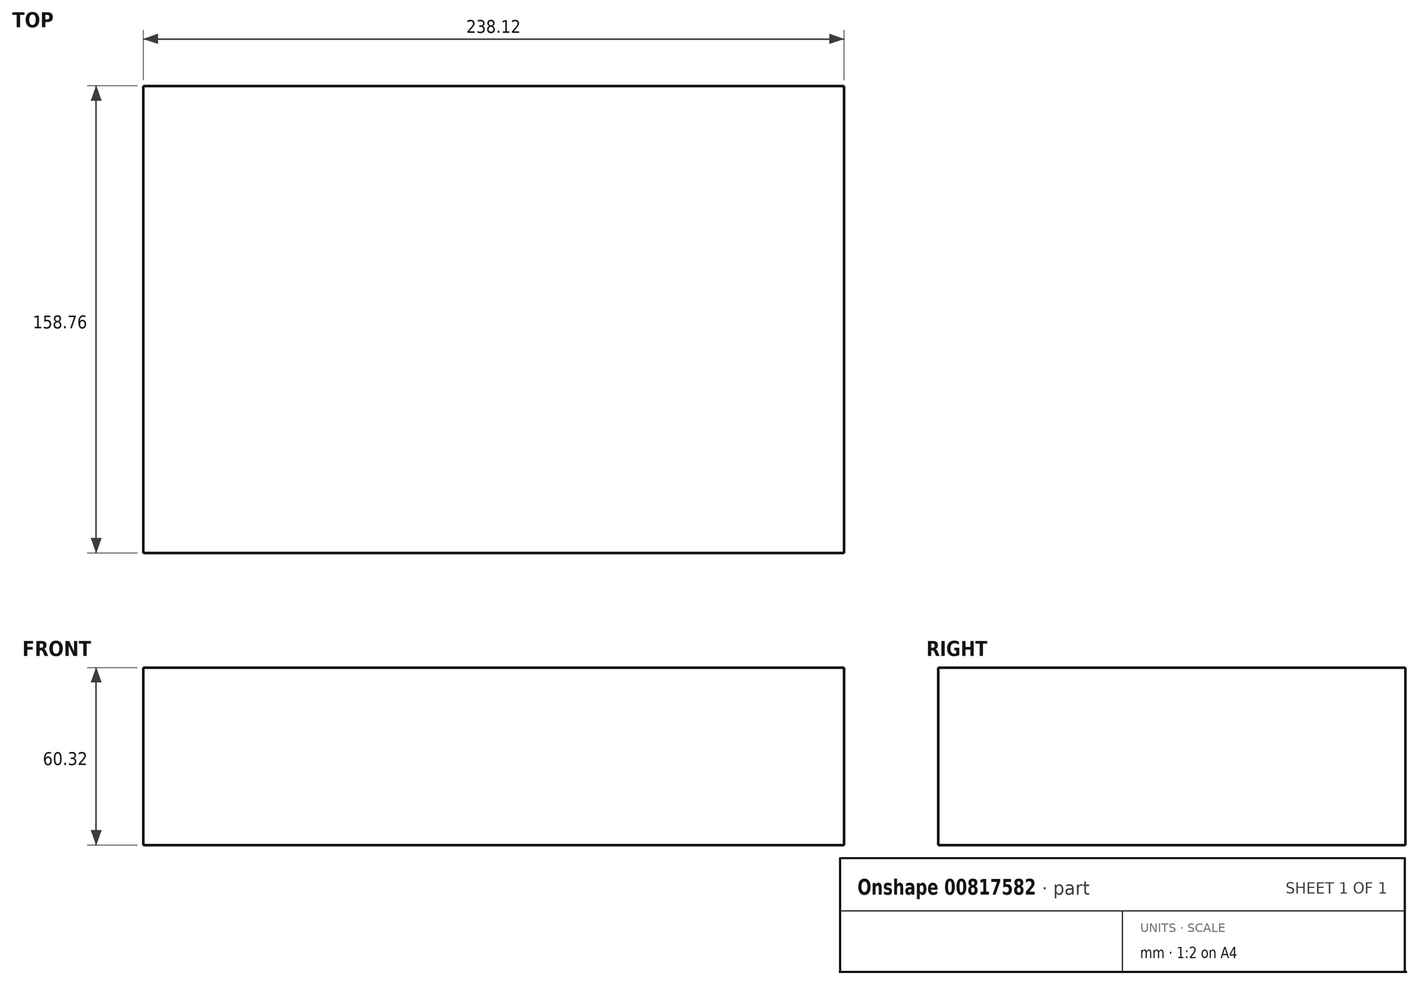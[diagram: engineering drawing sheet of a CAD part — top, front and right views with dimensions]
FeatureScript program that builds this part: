
annotation { "Feature Type Name" : "Feature", "Feature Type Description" : "" }
export const myFeature = defineFeature(function(context is Context, id is Id, definition is map)
    precondition{}
    {
        {
            var Q0;
            Q0=qCreatedBy(makeId("Top.planeOp"),FACE);
            var sketch = newSketch(context, id + "F0", { "sketchPlane" : qUnion([Q0])});
            skLineSegment(sketch, "E0.bottom", {"start": v(119.06, -79.37) * mm, "end": v(-119.06, -79.38) * mm});
            skLineSegment(sketch, "E0.top", {"start": v(119.06, 79.37) * mm, "end": v(-119.06, 79.37) * mm});
            skLineSegment(sketch, "E0.left", {"start": v(119.06, -79.37) * mm, "end": v(119.06, 79.38) * mm});
            skLineSegment(sketch, "E0.right", {"start": v(-119.06, -79.38) * mm, "end": v(-119.06, 79.38) * mm});
            skPoint(sketch, "E0.middle", {"position": v(0, 0) * mm});
            skSolve(sketch);
        }
        {
            var Q0;
            Q0=makeQuery(id+"F0.imprint","IMPRINT",FACE,{"disambiguationData":[TD([[makeQuery(id+"F0.imprint","IMPRINT",EDGE,{"derivedFrom":sQuery(id+"F0.wireOp",EDGE,"E0.bottom")}),-1.0]])]});
            extrude(context, id + "F1", {"entities" : qUnion([Q0]), "depth" : 60.32 * mm, "offsetDistance" : 25.4 * mm});
        }
    });
